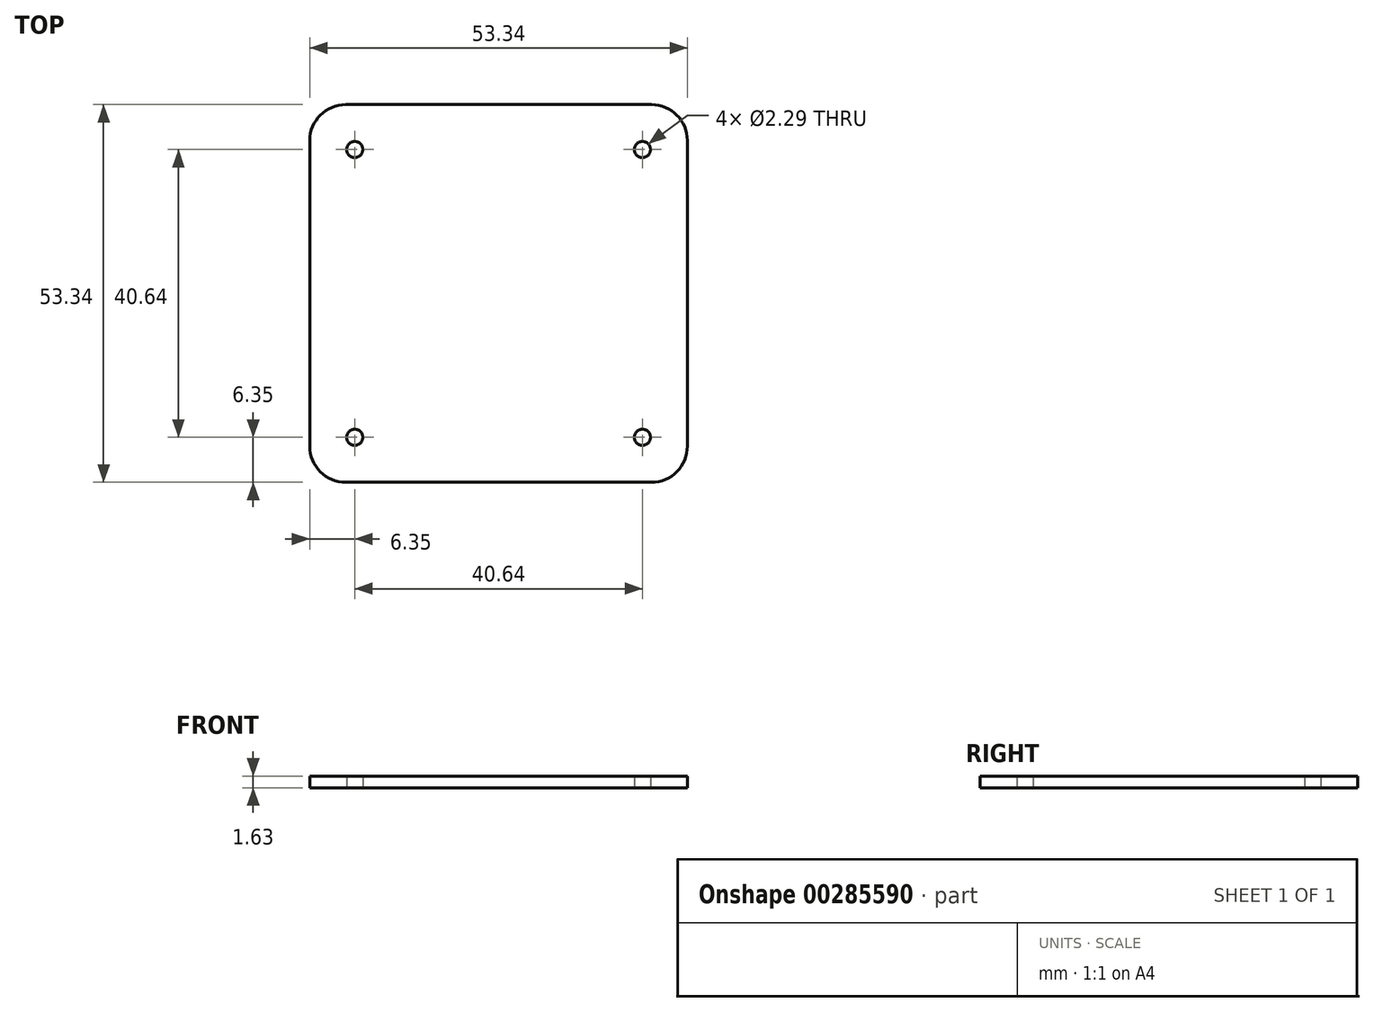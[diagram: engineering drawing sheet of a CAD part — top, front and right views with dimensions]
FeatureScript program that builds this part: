
annotation { "Feature Type Name" : "Feature", "Feature Type Description" : "" }
export const myFeature = defineFeature(function(context is Context, id is Id, definition is map)
    precondition{}
    {
        {
            var Q0;
            Q0=qCreatedBy(makeId("Top.planeOp"),FACE);
            var sketch = newSketch(context, id + "F0", { "sketchPlane" : qUnion([Q0])});
            skLineSegment(sketch, "E0.bottom", {"start": v(-21.59, 26.67) * mm, "end": v(21.6, 26.67) * mm});
            skLineSegment(sketch, "E0.top", {"start": v(-21.59, -26.67) * mm, "end": v(21.59, -26.67) * mm});
            skLineSegment(sketch, "E0.left", {"start": v(-26.67, 21.59) * mm, "end": v(-26.67, -21.59) * mm});
            skLineSegment(sketch, "E0.right", {"start": v(26.67, 21.59) * mm, "end": v(26.67, -21.6) * mm});
            skLineSegment(sketch, "E1", {"start": v(0, 26.67) * mm, "end": v(0, -26.67) * mm, "construction": true});
            skLineSegment(sketch, "E2", {"start": v(-26.67, 0) * mm, "end": v(26.67, 0) * mm, "construction": true});
            skPoint(sketch, "E2.endSnap0", {"position": v(26.67, 0) * mm});
            skPoint(sketch, "E3.visualSharp", {"position": v(-26.67, 26.67) * mm});
            skArc(sketch, "E3.filletArc", {"start": v(-21.59, 26.67) * mm, "mid": v(-25.18, 25.18) * mm, "end": v(-26.67, 21.59) * mm});
            skPoint(sketch, "E4.visualSharp", {"position": v(26.67, 26.67) * mm});
            skArc(sketch, "E4.filletArc", {"start": v(26.67, 21.59) * mm, "mid": v(25.18, 25.18) * mm, "end": v(21.6, 26.67) * mm});
            skPoint(sketch, "E5.visualSharp", {"position": v(26.67, -26.67) * mm});
            skArc(sketch, "E5.filletArc", {"start": v(21.59, -26.67) * mm, "mid": v(25.18, -25.18) * mm, "end": v(26.67, -21.6) * mm});
            skPoint(sketch, "E6.visualSharp", {"position": v(-26.67, -26.67) * mm});
            skArc(sketch, "E6.filletArc", {"start": v(-26.67, -21.6) * mm, "mid": v(-25.18, -25.18) * mm, "end": v(-21.59, -26.67) * mm});
            skCircle(sketch, "E7", {"center": v(-20.32, 20.32) * mm, "radius": 1.14 * mm});
            skCircle(sketch, "E8.MirrorC", {"center": v(20.32, 20.32) * mm, "radius": 1.14 * mm});
            skCircle(sketch, "E9.MirrorC", {"center": v(-20.32, -20.32) * mm, "radius": 1.14 * mm});
            skCircle(sketch, "E10.MirrorC", {"center": v(20.32, -20.32) * mm, "radius": 1.14 * mm});
            skSolve(sketch);
        }
        {
            var Q0;
            Q0=makeQuery(id+"F0.imprint","IMPRINT",FACE,{"disambiguationData":[TD([[makeQuery(id+"F0.imprint","IMPRINT",EDGE,{"derivedFrom":sQuery(id+"F0.wireOp",EDGE,"E0.bottom")}),-1.0]])]});
            extrude(context, id + "F1", {"entities" : qUnion([Q0]), "depth" : 1.63 * mm});
        }
    });
